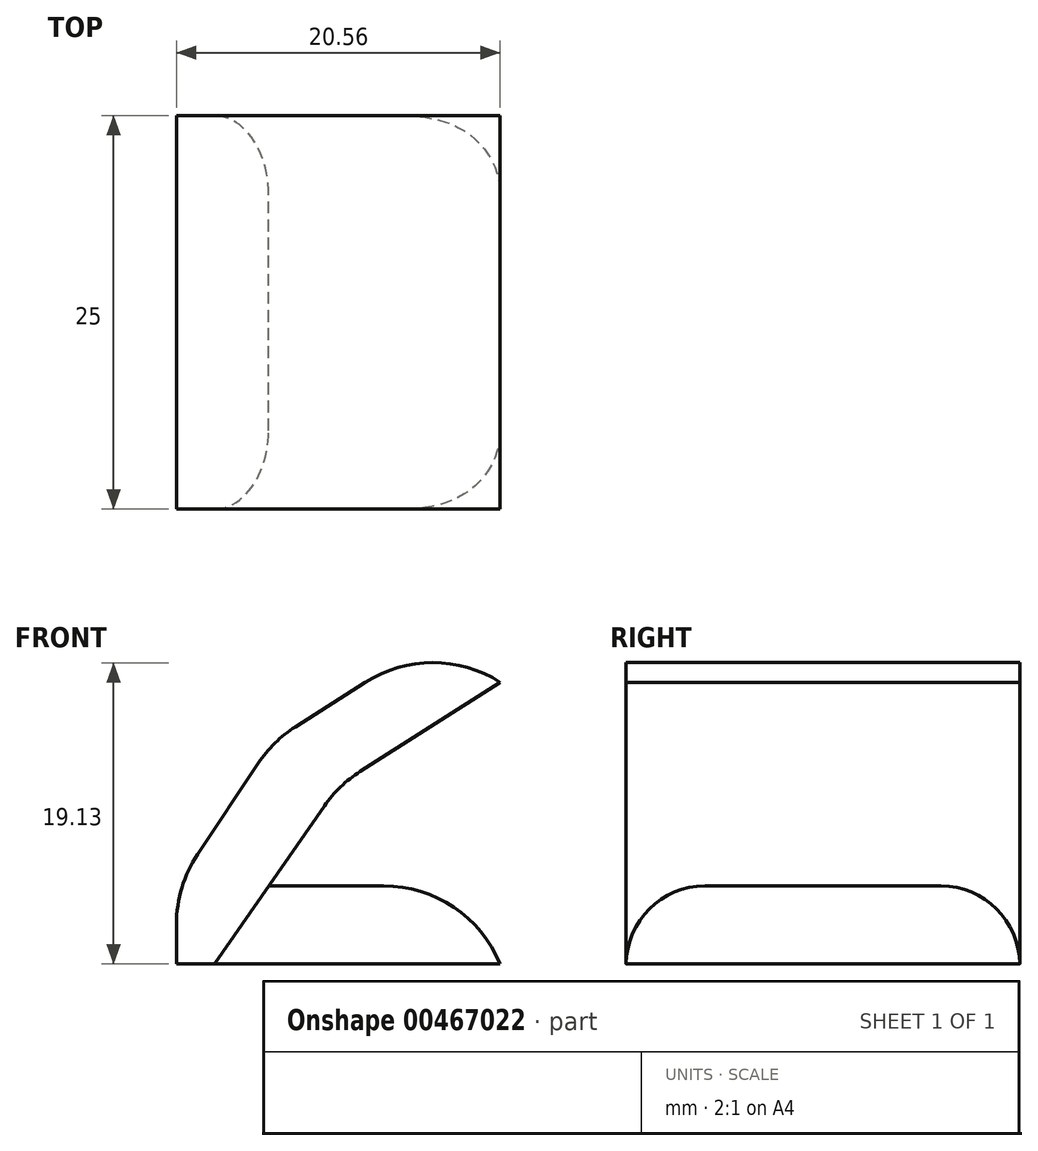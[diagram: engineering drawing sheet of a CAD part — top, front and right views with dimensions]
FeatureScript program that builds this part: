
annotation { "Feature Type Name" : "Feature", "Feature Type Description" : "" }
export const myFeature = defineFeature(function(context is Context, id is Id, definition is map)
    precondition{}
    {
        {
            var Q0;
            Q0=qCreatedBy(makeId("Front.planeOp"),FACE);
            var sketch = newSketch(context, id + "F0", { "sketchPlane" : qUnion([Q0])});
            skLineSegment(sketch, "E0", {"start": v(0, 0) * mm, "end": v(-20.56, 0) * mm});
            skLineSegment(sketch, "E1", {"start": v(-20.56, 0) * mm, "end": v(-20.56, 4.95) * mm});
            skLineSegment(sketch, "E2", {"start": v(-20.56, 4.95) * mm, "end": v(-14.43, 14.15) * mm});
            skLineSegment(sketch, "E3", {"start": v(-14.43, 14.15) * mm, "end": v(0, 23.35) * mm});
            skLineSegment(sketch, "E4", {"start": v(0, 0) * mm, "end": v(0, 4.95) * mm});
            skLineSegment(sketch, "E5", {"start": v(0, 4.95) * mm, "end": v(-14.7, 4.95) * mm});
            skLineSegment(sketch, "E6", {"start": v(-14.7, 4.95) * mm, "end": v(-10.24, 11.36) * mm});
            skLineSegment(sketch, "E7", {"start": v(-10.24, 11.36) * mm, "end": v(0, 17.9) * mm});
            skLineSegment(sketch, "E8", {"start": v(0, 17.9) * mm, "end": v(0, 23.35) * mm});
            skSolve(sketch);
        }
        {
            var Q0;
            Q0=makeQuery(id+"F0.imprint","IMPRINT",FACE,{"disambiguationData":[TD([[makeQuery(id+"F0.imprint","IMPRINT",EDGE,{"derivedFrom":sQuery(id+"F0.wireOp",EDGE,"E0")}),-1.0]])]});
            extrude(context, id + "F1", {"entities" : qUnion([Q0]), "endBound" : BoundingType.SYMMETRIC, "depth" : 25 * mm, "offsetDistance" : 25 * mm});
        }
        {
            var Q0;
            Q0=makeQuery(id+"F1.opExtrude","SWEPT_EDGE",EDGE,{"disambiguationData":[OSD([sQuery(id+"F0.wireOp",EDGE,"E3"),sQuery(id+"F0.wireOp",EDGE,"E8")])]});
            var Q1;
            Q1=makeQuery(id+"F1.opExtrude","SWEPT_EDGE",EDGE,{"disambiguationData":[OSD([sQuery(id+"F0.wireOp",EDGE,"E2"),sQuery(id+"F0.wireOp",EDGE,"E3")])]});
            var Q2;
            Q2=makeQuery(id+"F1.opExtrude","SWEPT_EDGE",EDGE,{"disambiguationData":[OSD([sQuery(id+"F0.wireOp",EDGE,"E1"),sQuery(id+"F0.wireOp",EDGE,"E2")])]});
            var Q3;
            Q3=makeQuery(id+"F1.opExtrude","SWEPT_EDGE",EDGE,{"disambiguationData":[OSD([sQuery(id+"F0.wireOp",EDGE,"E4"),sQuery(id+"F0.wireOp",EDGE,"E5")])]});
            fillet(context, id + "F2", {"entities" : qUnion([Q0, Q1, Q2, Q3]), "tangentPropagation" : true, "radius" : 8 * mm, "defaultsChanged" : true, "vertexSettings" : [], "allowEdgeOverflow" : false});
        }
        {
            var Q0;
            {var subQ0=sQuery(id+"F0.wireOp",EDGE,"E5");var subQ1=sQuery(id+"F0.wireOp",EDGE,"E4");Q0=makeQuery(id+"F2.opFillet","BLEND_EDGE",EDGE,{"blendedFrom":[makeQuery(id+"F1.opExtrude","SWEPT_EDGE",EDGE,{"disambiguationData":[OSD([subQ1,subQ0])]}),makeQuery(id+"F1.opExtrude","CAP_FACE",FACE,{"disambiguationData":[OSD([sQuery(id+"F0.wireOp",EDGE,"E0"),sQuery(id+"F0.wireOp",EDGE,"E1"),sQuery(id+"F0.wireOp",EDGE,"E2"),sQuery(id+"F0.wireOp",EDGE,"E3"),subQ1,subQ0,sQuery(id+"F0.wireOp",EDGE,"E6"),sQuery(id+"F0.wireOp",EDGE,"E7"),sQuery(id+"F0.wireOp",EDGE,"E8")])],"isStart":true})],"blendedInto":[makeQuery(id+"F1.opExtrude","CAP_FACE",FACE,{"disambiguationData":[OSD([sQuery(id+"F0.wireOp",EDGE,"E0"),sQuery(id+"F0.wireOp",EDGE,"E1"),sQuery(id+"F0.wireOp",EDGE,"E2"),sQuery(id+"F0.wireOp",EDGE,"E3"),subQ1,subQ0,sQuery(id+"F0.wireOp",EDGE,"E6"),sQuery(id+"F0.wireOp",EDGE,"E7"),sQuery(id+"F0.wireOp",EDGE,"E8")])],"isStart":true})]});}
            var Q1;
            {var subQ0=sQuery(id+"F0.wireOp",EDGE,"E5");var subQ1=sQuery(id+"F0.wireOp",EDGE,"E4");Q1=makeQuery(id+"F2.opFillet","BLEND_EDGE",EDGE,{"blendedFrom":[makeQuery(id+"F1.opExtrude","SWEPT_EDGE",EDGE,{"disambiguationData":[OSD([subQ1,subQ0])]}),makeQuery(id+"F1.opExtrude","CAP_FACE",FACE,{"disambiguationData":[OSD([sQuery(id+"F0.wireOp",EDGE,"E0"),sQuery(id+"F0.wireOp",EDGE,"E1"),sQuery(id+"F0.wireOp",EDGE,"E2"),sQuery(id+"F0.wireOp",EDGE,"E3"),subQ1,subQ0,sQuery(id+"F0.wireOp",EDGE,"E6"),sQuery(id+"F0.wireOp",EDGE,"E7"),sQuery(id+"F0.wireOp",EDGE,"E8")])],"isStart":false})],"blendedInto":[makeQuery(id+"F1.opExtrude","CAP_FACE",FACE,{"disambiguationData":[OSD([sQuery(id+"F0.wireOp",EDGE,"E0"),sQuery(id+"F0.wireOp",EDGE,"E1"),sQuery(id+"F0.wireOp",EDGE,"E2"),sQuery(id+"F0.wireOp",EDGE,"E3"),subQ1,subQ0,sQuery(id+"F0.wireOp",EDGE,"E6"),sQuery(id+"F0.wireOp",EDGE,"E7"),sQuery(id+"F0.wireOp",EDGE,"E8")])],"isStart":false})]});}
            fillet(context, id + "F3", {"entities" : qUnion([Q0, Q1]), "tangentPropagation" : true, "radius" : 5 * mm, "defaultsChanged" : false, "vertexSettings" : [], "allowEdgeOverflow" : false});
        }
        {
            var Q0;
            Q0=makeQuery(id+"F1.opExtrude","SWEPT_EDGE",EDGE,{"disambiguationData":[OSD([sQuery(id+"F0.wireOp",EDGE,"E6"),sQuery(id+"F0.wireOp",EDGE,"E7")])]});
            fillet(context, id + "F4", {"entities" : qUnion([Q0]), "tangentPropagation" : true, "radius" : 8 * mm, "defaultsChanged" : true, "vertexSettings" : [], "allowEdgeOverflow" : false});
        }
    });
